# Revit family: Single Container Bracket Assy-JCI_Sapphire_Plus-(70 bar) Novec1230
name_source: partatom
category: Specialty Equipment
revit_build: Autodesk Revit 2017 (Build: 20171027_0315(x64)
units: mm (PartAtom-declared; Revit-internal decimal feet)

## family parameters
Always vertical = No
Cut with Voids When Loaded = No
OmniClass Number = 23.29.33.13.11
Part Type = Normal
Room Calculation Point = No
Round Connector Dimension = Use Diameter
Shared = No
Work Plane-Based = Yes

## types (5) — shared parameters
Date Modified = YYYY/MM/DD
Description = Container Bracket Assembly-Sapphire Plus
Diameter = 47.6 mm  [stored 0.156168 ft]
Discharge Flow = 0 GPM
Equipment Abbreviation = CB
Equipment Number = XXX
Family Version = 1.0
Fire Suppression Agent = 3M™ Novec™ 1230 Fire Protection Fluid
Height = 41 mm  [stored 0.134514 ft]
Length = 47.6 mm  [stored 0.156168 ft]
Manufacturer = Johnson Controls, Inc.
Model Disclaimer = For More Information Contact JOHNSON CONTROLS
Pipe Diameter = 12.7 mm  [stored 0.0416667 ft]
URL = http://www.sapphireplus.com
Upper Brackets Mounting Height = 200 mm  [stored 0.656168 ft]
Width = 47.6 mm  [stored 0.156168 ft]
zero-valued in all types: Default Elevation, Lower Brackets Mounting Height

## per-type parameters (varying)
| type | CONTAINER BRACKET ASSY TYPE | Material | Model | Part Number |
| 15 L | Container Bracket-JCI_Sapphire_Plus-(70 bar)Novec1230 : 15 L | JCI - Metal - Steel | 311700002 | 311700002 |
| 30 L | Container Bracket-JCI_Sapphire_Plus-(70 bar)Novec1230 : 30 L | JCI - Metal - Brass - Satin | 311700003 | 311700003 |
| 34-45-60-80 L | Container Bracket-JCI_Sapphire_Plus-(70 bar)Novec1230 : 15 L | JCI - Metal - Steel | 311700004 | 311700004 |
| 120-150 L | Container Bracket-JCI_Sapphire_Plus-(70 bar)Novec1230 : 120-150 L | JCI - Metal - Brass - Satin | 311700005 | 311700005 |
| PESO 120-180 L | Container Bracket-JCI_Sapphire_Plus-(70 bar)Novec1230 : PESO 120-180 L | JCI - Metal - Brass - Satin | 311700006 | 311700006 |

note: [stored X ft] marks values corroborated as IEEE doubles in the binary element streams (Revit-internal decimal feet)

## geometry (parser evidence)
native form markers: Sweep x7
no freeform markers — native parametric forms only
